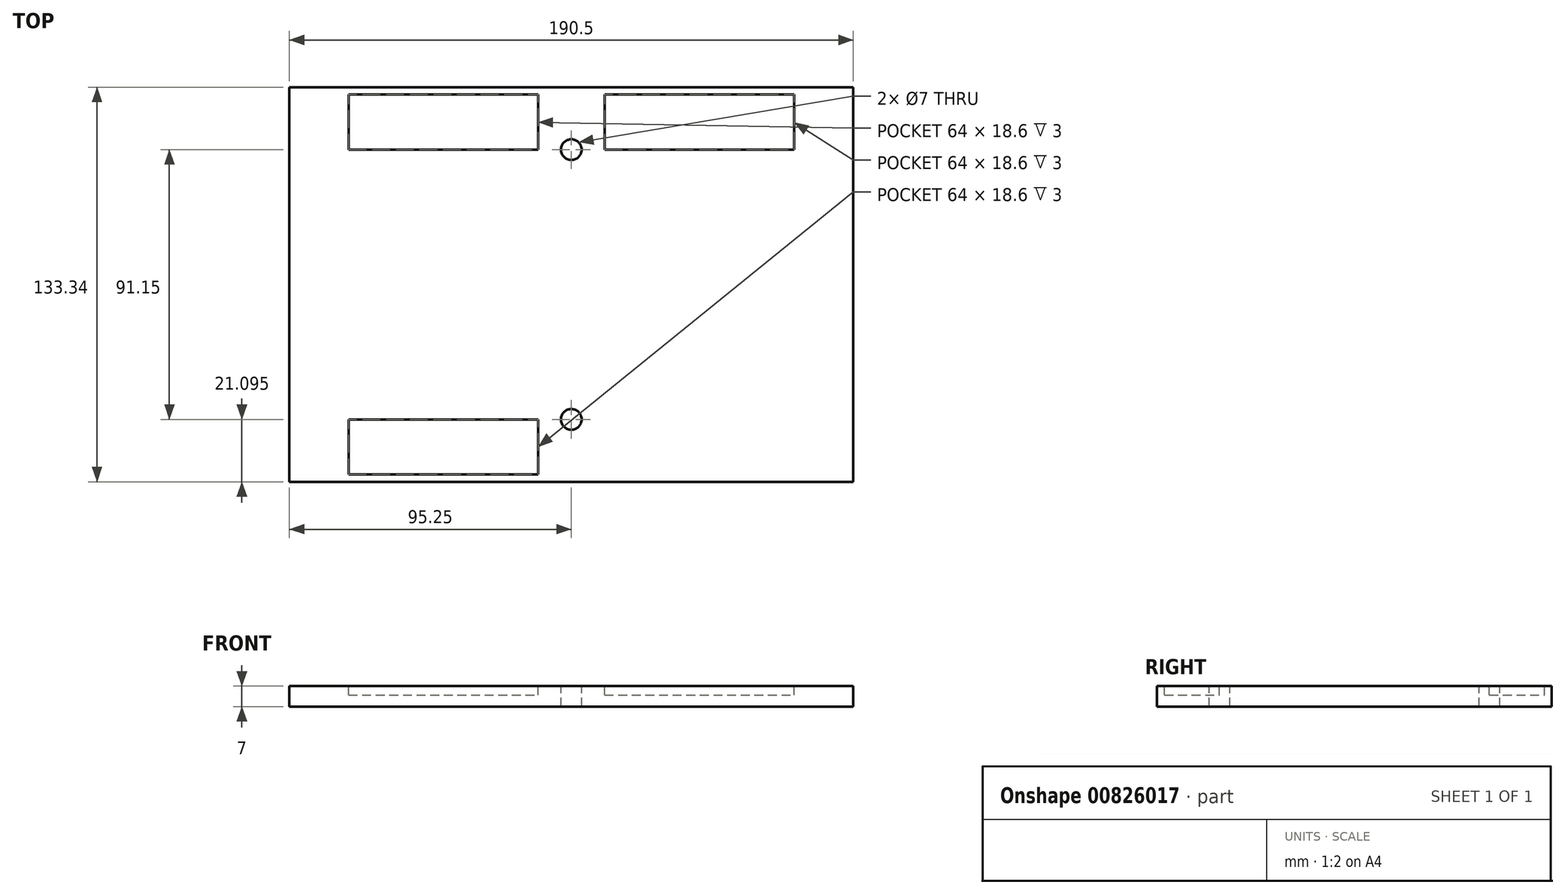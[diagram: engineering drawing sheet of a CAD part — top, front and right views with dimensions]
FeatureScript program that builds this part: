
annotation { "Feature Type Name" : "Feature", "Feature Type Description" : "" }
export const myFeature = defineFeature(function(context is Context, id is Id, definition is map)
    precondition{}
    {
        {
            var Q0;
            Q0=qCreatedBy(makeId("Top.planeOp"),FACE);
            var sketch = newSketch(context, id + "F0", { "sketchPlane" : qUnion([Q0])});
            skLineSegment(sketch, "E0.bottom", {"start": v(95.25, -66.67) * mm, "end": v(-95.25, -66.68) * mm});
            skLineSegment(sketch, "E0.top", {"start": v(95.25, 66.68) * mm, "end": v(-95.25, 66.67) * mm});
            skLineSegment(sketch, "E0.left", {"start": v(95.25, -66.67) * mm, "end": v(95.25, 66.68) * mm});
            skLineSegment(sketch, "E0.right", {"start": v(-95.25, -66.68) * mm, "end": v(-95.25, 66.67) * mm});
            skPoint(sketch, "E0.middle", {"position": v(0, 0) * mm});
            skSolve(sketch);
        }
        {
            var Q0;
            Q0=makeQuery(id+"F0.imprint","IMPRINT",FACE,{"disambiguationData":[TD([[makeQuery(id+"F0.imprint","IMPRINT",EDGE,{"derivedFrom":sQuery(id+"F0.wireOp",EDGE,"E0.bottom")}),-1.0]])]});
            extrude(context, id + "F1", {"entities" : qUnion([Q0]), "depth" : 7 * mm, "offsetDistance" : 25.4 * mm});
        }
        {
            var Q0;
            Q0=makeQuery(id+"F1.opExtrude","CAP_FACE",FACE,{"disambiguationData":[OSD([sQuery(id+"F0.wireOp",EDGE,"E0.bottom"),sQuery(id+"F0.wireOp",EDGE,"E0.top"),sQuery(id+"F0.wireOp",EDGE,"E0.left"),sQuery(id+"F0.wireOp",EDGE,"E0.right")])],"isStart":false});
            var sketch = newSketch(context, id + "F2", { "sketchPlane" : qUnion([Q0])});
            skLineSegment(sketch, "E1", {"start": v(-95.25, 66.67) * mm, "end": v(-75.25, 66.67) * mm});
            skLineSegment(sketch, "E2", {"start": v(-75.25, -66.68) * mm, "end": v(-75.25, 66.68) * mm});
            skLineSegment(sketch, "E3", {"start": v(95.25, 66.68) * mm, "end": v(75.25, 66.68) * mm});
            skLineSegment(sketch, "E4", {"start": v(75.25, -66.67) * mm, "end": v(75.25, 66.68) * mm});
            skLineSegment(sketch, "E5", {"start": v(-95.25, 66.67) * mm, "end": v(-95.25, 64.17) * mm});
            skLineSegment(sketch, "E6", {"start": v(95.25, 64.17) * mm, "end": v(-95.25, 64.17) * mm});
            skLineSegment(sketch, "E7", {"start": v(-95.25, -66.68) * mm, "end": v(-95.25, -64.18) * mm});
            skLineSegment(sketch, "E8", {"start": v(95.25, -64.18) * mm, "end": v(-95.25, -64.18) * mm});
            skLineSegment(sketch, "E9.bottom", {"start": v(-75.25, -64.18) * mm, "end": v(-11.25, -64.18) * mm});
            skLineSegment(sketch, "E9.top", {"start": v(-75.25, -45.58) * mm, "end": v(-11.25, -45.58) * mm});
            skLineSegment(sketch, "E9.left", {"start": v(-75.25, -64.18) * mm, "end": v(-75.25, -45.58) * mm});
            skLineSegment(sketch, "E9.right", {"start": v(-11.25, -64.18) * mm, "end": v(-11.25, -45.58) * mm});
            skLineSegment(sketch, "E10", {"start": v(-11.25, -45.58) * mm, "end": v(75.25, -45.58) * mm});
            skLineSegment(sketch, "E11", {"start": v(75.25, -45.58) * mm, "end": v(75.25, -64.18) * mm});
            skLineSegment(sketch, "E12", {"start": v(75.25, -64.18) * mm, "end": v(11.25, -64.18) * mm});
            skLineSegment(sketch, "E13", {"start": v(11.25, -64.18) * mm, "end": v(11.25, -45.58) * mm});
            skLineSegment(sketch, "E14", {"start": v(-11.25, -45.58) * mm, "end": v(-11.25, 64.17) * mm});
            skLineSegment(sketch, "E15", {"start": v(-11.25, 64.17) * mm, "end": v(11.25, 64.17) * mm});
            skLineSegment(sketch, "E16", {"start": v(11.25, 64.17) * mm, "end": v(11.25, -45.58) * mm});
            skLineSegment(sketch, "E17", {"start": v(-11.25, 64.17) * mm, "end": v(-11.25, 45.57) * mm});
            skLineSegment(sketch, "E18", {"start": v(-75.25, 45.57) * mm, "end": v(-11.25, 45.57) * mm});
            skLineSegment(sketch, "E19", {"start": v(11.25, 45.57) * mm, "end": v(75.25, 45.57) * mm});
            skLineSegment(sketch, "E20.left", {"start": v(-75.25, -45.58) * mm, "end": v(-75.25, -64.18) * mm});
            skLineSegment(sketch, "E20.right", {"start": v(-11.25, -45.58) * mm, "end": v(-11.25, -64.18) * mm});
            skLineSegment(sketch, "E21.bottom", {"start": v(11.25, -45.58) * mm, "end": v(75.25, -45.58) * mm});
            skLineSegment(sketch, "E21.top", {"start": v(11.25, -64.18) * mm, "end": v(75.25, -64.18) * mm});
            skLineSegment(sketch, "E21.left", {"start": v(11.25, -45.58) * mm, "end": v(11.25, -64.18) * mm});
            skLineSegment(sketch, "E22.top", {"start": v(11.25, 64.18) * mm, "end": v(75.25, 64.18) * mm});
            skLineSegment(sketch, "E22.left", {"start": v(11.25, 45.57) * mm, "end": v(11.25, 64.18) * mm});
            skLineSegment(sketch, "E22.right", {"start": v(75.25, 45.57) * mm, "end": v(75.25, 64.18) * mm});
            skLineSegment(sketch, "E23.top", {"start": v(-75.25, 64.17) * mm, "end": v(-11.25, 64.17) * mm});
            skLineSegment(sketch, "E23.left", {"start": v(-75.25, 45.57) * mm, "end": v(-75.25, 64.17) * mm});
            skLineSegment(sketch, "E23.right", {"start": v(-11.25, 45.57) * mm, "end": v(-11.25, 64.17) * mm});
            skSolve(sketch);
        }
        {
            var Q0;
            Q0=makeQuery(id+"F2.imprint","IMPRINT",FACE,{"disambiguationData":[TD([[makeQuery(id+"F2.imprint","IMPRINT",EDGE,{"derivedFrom":sQuery(id+"F2.wireOp",EDGE,"E18")}),1.0]])]});
            var Q1;
            Q1=makeQuery(id+"F2.imprint","IMPRINT",FACE,{"disambiguationData":[TD([[makeQuery(id+"F2.imprint","IMPRINT",EDGE,{"derivedFrom":sQuery(id+"F2.wireOp",EDGE,"E19")}),1.0]])]});
            var Q2;
            Q2=makeQuery(id+"F2.imprint","IMPRINT",FACE,{"disambiguationData":[TD([[makeQuery(id+"F2.imprint","IMPRINT",EDGE,{"derivedFrom":sQuery(id+"F2.wireOp",EDGE,"E21.bottom")}),-1.0]])]});
            var Q3;
            Q3=makeQuery(id+"F2.imprint","IMPRINT",FACE,{"disambiguationData":[TD([[makeQuery(id+"F2.imprint","IMPRINT",EDGE,{"derivedFrom":sQuery(id+"F2.wireOp",EDGE,"E9.top")}),-1.0]])]});
            extrude(context, id + "F3", {"entities" : qUnion([Q0, Q1, Q2, Q3]), "operationType" : NewBodyOperationType.REMOVE, "oppositeDirection" : true, "depth" : 3 * mm, "offsetDistance" : 25 * mm});
        }
        {
            var Q0;
            Q0=makeQuery(id+"F1.opExtrude","CAP_FACE",FACE,{"disambiguationData":[OSD([sQuery(id+"F0.wireOp",EDGE,"E0.bottom"),sQuery(id+"F0.wireOp",EDGE,"E0.top"),sQuery(id+"F0.wireOp",EDGE,"E0.left"),sQuery(id+"F0.wireOp",EDGE,"E0.right")])],"isStart":false});
            var sketch = newSketch(context, id + "F4", { "sketchPlane" : qUnion([Q0])});
            skLineSegment(sketch, "E24", {"start": v(11.25, 64.17) * mm, "end": v(11.25, 45.57) * mm});
            skLineSegment(sketch, "E25", {"start": v(11.25, -64.18) * mm, "end": v(11.25, -45.58) * mm});
            skPoint(sketch, "E26.end.orphan", {"position": v(-11.25, 45.57) * mm});
            skPoint(sketch, "E27.orphan", {"position": v(-11.25, -45.58) * mm});
            skCircle(sketch, "E28", {"center": v(0, -45.58) * mm, "radius": 3.5 * mm});
            skCircle(sketch, "E29", {"center": v(0, 45.57) * mm, "radius": 3.5 * mm});
            skPoint(sketch, "E30.center.orphan", {"position": v(0, -54.88) * mm});
            skPoint(sketch, "E31.center.orphan", {"position": v(0, 54.87) * mm});
            skSolve(sketch);
        }
        {
            var Q0;
            Q0 = qSketchRegion(id + "F4", true);
            extrude(context, id + "F5", {"entities" : qUnion([Q0]), "operationType" : NewBodyOperationType.REMOVE, "oppositeDirection" : true, "depth" : 25 * mm, "offsetDistance" : 25 * mm});
        }
    });
